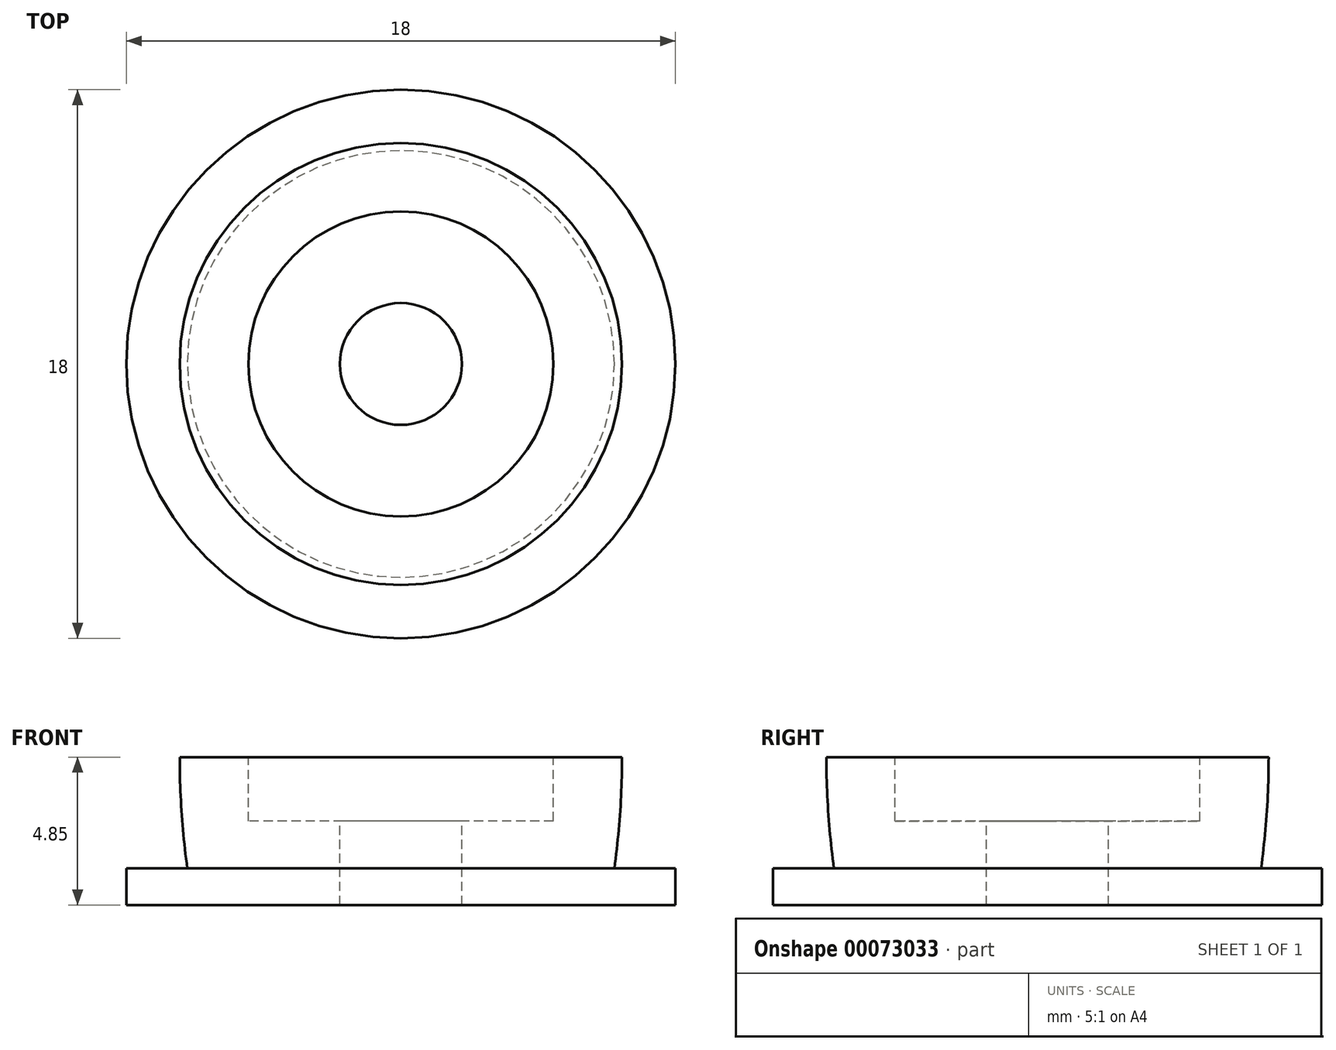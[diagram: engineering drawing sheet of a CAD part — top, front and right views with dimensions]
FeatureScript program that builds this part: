
annotation { "Feature Type Name" : "Feature", "Feature Type Description" : "" }
export const myFeature = defineFeature(function(context is Context, id is Id, definition is map)
    precondition{}
    {
        {
            var Q0;
            Q0=qCreatedBy(makeId("Front.planeOp"),FACE);
            var sketch = newSketch(context, id + "F0", { "sketchPlane" : qUnion([Q0])});
            skLineSegment(sketch, "E0", {"start": v(2, 0) * mm, "end": v(2, 2.75) * mm});
            skLineSegment(sketch, "E1", {"start": v(2, 2.75) * mm, "end": v(5, 2.75) * mm});
            skLineSegment(sketch, "E2", {"start": v(5, 2.75) * mm, "end": v(5, 4.85) * mm});
            skLineSegment(sketch, "E3", {"start": v(5, 4.85) * mm, "end": v(7.25, 4.85) * mm});
            skLineSegment(sketch, "E4", {"start": v(7, 1.2) * mm, "end": v(9, 1.2) * mm});
            skLineSegment(sketch, "E5", {"start": v(9, 1.2) * mm, "end": v(9, 0) * mm});
            skLineSegment(sketch, "E6", {"start": v(9, 0) * mm, "end": v(2, 0) * mm});
            skLineSegment(sketch, "E7", {"start": v(0, 4.86) * mm, "end": v(0, -4.46) * mm, "construction": true});
            skArc(sketch, "E8", {"start": v(7.25, 4.85) * mm, "mid": v(7.19, 3.02) * mm, "end": v(7, 1.2) * mm});
            skSolve(sketch);
        }
        {
            var Q0;
            Q0 = qSketchRegion(id + "F0", true);
            var Q1;
            Q1=sQuery(id+"F0.wireOp",EDGE,"E7");
            revolve(context, id + "F1", {"entities" : qUnion([Q0]), "axis" : qUnion([Q1]), "revolveType" : RevolveType.FULL});
        }
    });
